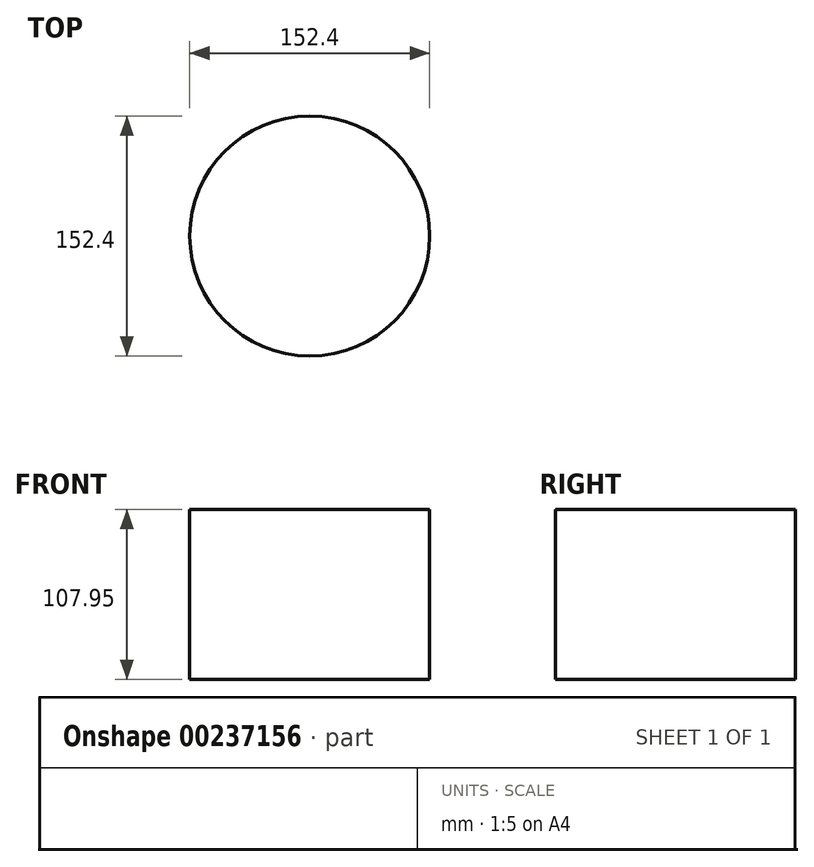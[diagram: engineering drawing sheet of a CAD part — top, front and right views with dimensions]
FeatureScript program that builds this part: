
annotation { "Feature Type Name" : "Feature", "Feature Type Description" : "" }
export const myFeature = defineFeature(function(context is Context, id is Id, definition is map)
    precondition{}
    {
        {
            var Q0;
            Q0=qCreatedBy(makeId("Top.planeOp"),FACE);
            var sketch = newSketch(context, id + "F0", { "sketchPlane" : qUnion([Q0])});
            skCircle(sketch, "E0", {"center": v(0, 0) * mm, "radius": 76.2 * mm});
            skSolve(sketch);
        }
        {
            var Q0;
            Q0 = qSketchRegion(id + "F0", true);
            extrude(context, id + "F1", {"entities" : qUnion([Q0]), "depth" : 107.95 * mm});
        }
        {
            var Q0;
            Q0=qCreatedBy(makeId("Top.planeOp"),FACE);
            var sketch = newSketch(context, id + "F2", { "sketchPlane" : qUnion([Q0])});
            skCircle(sketch, "E1", {"center": v(-136.14, 110) * mm, "radius": 15.82 * mm});
            skSolve(sketch);
        }
        {
            var Q0;
            Q0 = qSketchRegion(id + "F2", true);
            extrude(context, id + "F3", {"entities" : qUnion([Q0]), "operationType" : NewBodyOperationType.REMOVE, "oppositeDirection" : true, "depth" : 235.2 * mm});
        }
        {
            var Q0;
            Q0=qCreatedBy(makeId("Top.planeOp"),FACE);
            var sketch = newSketch(context, id + "F4", { "sketchPlane" : qUnion([Q0])});
            skCircle(sketch, "E2", {"center": v(0, 0) * mm, "radius": 29.43 * mm});
            skSolve(sketch);
        }
        {
            var Q0;
            Q0 = qSketchRegion(id + "F4", true);
            extrude(context, id + "F5", {"entities" : qUnion([Q0]), "operationType" : NewBodyOperationType.REMOVE, "oppositeDirection" : true, "depth" : 293.12 * mm});
        }
    });
